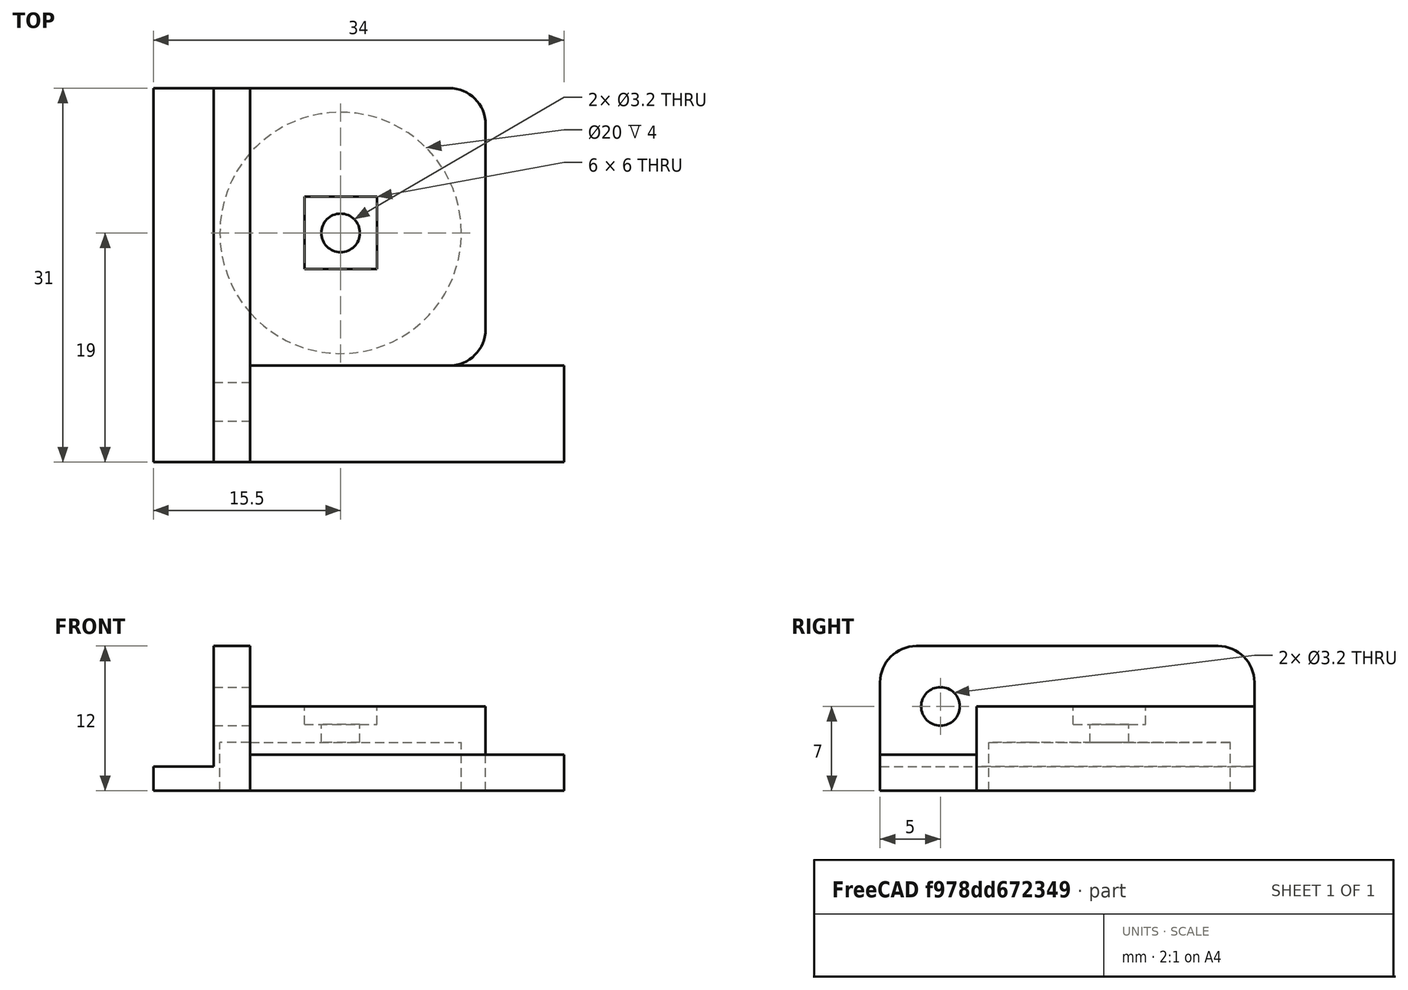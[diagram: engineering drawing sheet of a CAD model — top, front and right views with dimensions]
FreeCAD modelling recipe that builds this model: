
FCSTD DOCUMENT  (FreeCAD 0.18R14555 (Git shallow))
Label: ckd-router-magnet
License: All rights reserved
LicenseURL: http://en.wikipedia.org/wiki/All_rights_reserved
objects: Part::Box×6, Part::Cut×6, Part::Cylinder×4, Part::MultiFuse×2, Part::Fillet×2, Part::Feature×1
note: 21 computed .brp shape members not serialized (recipe doc carries the construction recipe); baked Part::Feature solids carry a one-line shape summary decoded from their .brp

FEATURE [Part::Box] Box  label="Cube"
  AttacherType = Attacher::AttachEngine3D
  Height = 2
  Length = 5
  Placement = pos=(-8,0,0) rot=(0,0,1;0rad)
  Width = 31
FEATURE [Part::Box] Box001  label="Cube001"
  AttacherType = Attacher::AttachEngine3D
  Height = 3
  Length = 26
  Width = 8
FEATURE [Part::Box] Box002  label="Cube002"
  AttacherType = Attacher::AttachEngine3D
  Height = 12
  Length = 3
  Placement = pos=(-3,0,0) rot=(0,0,1;0rad)
  Width = 31
FEATURE [Part::Cylinder] Cylinder
  Angle = 360
  AttacherType = Attacher::AttachEngine3D
  Height = 4
  Placement = pos=(13,19,0) rot=(0,0,1;0rad)
  Radius = 10
FEATURE [Part::Cylinder] Cylinder002
  Angle = 360
  AttacherType = Attacher::AttachEngine3D
  Height = 3
  Placement = pos=(-3,5,7) rot=(0,1,0;1.5708rad)
  Radius = 1.6
FEATURE [Part::Cylinder] Cylinder003
  Angle = 360
  AttacherType = Attacher::AttachEngine3D
  Height = 10
  Placement = pos=(13,19,0) rot=(0,0,1;0rad)
  Radius = 1.6
FEATURE [Part::Box] Box003  label="Cube003"
  AttacherType = Attacher::AttachEngine3D
  Height = 7
  Length = 25
  Placement = pos=(0,8,0) rot=(0,0,1;0rad)
  Width = 23
FEATURE [Part::MultiFuse] Fusion
  Shapes = -> [Box002,Box]
FEATURE [Part::Cut] Cut
  Base = -> Fusion
  Tool = -> Cylinder002
FEATURE [Part::Cut] Cut001
  Base = -> Box003
  Tool = -> Cylinder
FEATURE [Part::Box] Box004  label="Cube004"
  AttacherType = Attacher::AttachEngine3D
  Height = 2
  Length = 6
  Placement = pos=(10,16,5.5) rot=(0,0,1;0rad)
  Width = 6
FEATURE [Part::Cut] Cut002
  Base = -> Cut001
  Tool = -> Box004
FEATURE [Part::Cut] Cut003
  Base = -> Cut002
  Placement = pos=(-3,0,0) rot=(0,0,1;0rad)
  Tool = -> Cylinder003
FEATURE [Part::Fillet] Fillet001
  Base = -> Cut003
  Edges = 2 edges r=3: [Edge6,Edge15]
  Placement = pos=(-2.5,0,0) rot=(0,0,1;0rad)
FEATURE [Part::Box] Box005  label="Cube005"
  AttacherType = Attacher::AttachEngine3D
  Height = 5
  Length = 3
  Placement = pos=(-6,0,2) rot=(0,0,1;0rad)
  Width = 31
FEATURE [Part::Cut] Cut004
  Base = -> Fillet001
  Tool = -> Box005
FEATURE [Part::Cylinder] Cylinder004
  Angle = 360
  AttacherType = Attacher::AttachEngine3D
  Height = 4
  Placement = pos=(7.5,19,0) rot=(0,0,1;0rad)
  Radius = 10
FEATURE [Part::MultiFuse] Fusion001
  Shapes = -> [Cut004,Cut]
FEATURE [Part::Cut] Cut005
  Base = -> Fusion001
  Tool = -> Cylinder004
FEATURE [Part::Fillet] Fillet
  Base = -> Cut005
  Edges = 2 edges r=3: [Edge40,Edge41]
FEATURE [Part::Feature] Fillet002
  shape: bbox 27.5 x 31 x 12 mm, 24 faces (baked)
